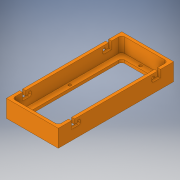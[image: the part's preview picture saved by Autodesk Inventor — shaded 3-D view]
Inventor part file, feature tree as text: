
AUTODESK INVENTOR PART (.ipt)
format: ipt  version: 2017 (Build 210142000, 142)  size: 281,088 bytes
history: native  units: in
note: dims shown in document units (in); Inventor stores cm internally (conversion verified against a paired STEP export)
features: extrude x4, sketch x3, fillet x3, plane x2, mirror x1, projected_geometry x1
ambient origin geometry x8: Origin, YZ Plane, XZ Plane, XY Plane, X Axis, Y Axis, Z Axis, Center Point
bodies: Solid1 (feature_tree)
feature tree (14):
  extrude  "Extrusion1"  Depth=0.125in
  sketch  "Sketch2"  dims[d2=0.125in d3=0.125in]
  extrude  "Extrusion9"  Depth=0.125in
  extrude  "Extrusion10"  Depth=0.125in
  extrude  "Extrusion11"  Depth=0.125in
  fillet  "Fillet1"  Radius=0.25in
  fillet  "Fillet2"  Radius=0.25in
  fillet  "Fillet3"  Radius=0.125in
  plane  "Work Plane1"
  mirror  "Mirror1"
  sketch  "Sketch9"  dims[d7=0.25in d8=0.125in]
  sketch  "Sketch10"  dims[d9=0.125in d10=0.125in d11=0.125in d12=0.25in d13=0.25in d14=0.125in d15=0.125in d16=0.25in d17=0.25in d18=0.125in d19=0.75in d20=0.0in d121=0.574in d154=1.0in d155=0.0in d156=0.25in d157=0.25in d158=0.25in d159=0.25in d160=0.125in d161=0.0in d163=0.125in d166=0.125in d167=4.75in d168=2.375in d169=0.125in d170=0.0625in d171=2.375in d172=0.125in d173=0.125in d174=1.75in d175=0.875in d176=0.125in d177=0.125in d178=0.9375in d179=0.125in d180=0.0in d181=0.125in d182=0.125in d183=0.125in d190=0.125in d191=0.125in d192=0.125in d193=0.125in d194=0.1in d195=0.1in d196=0.0625in d197=0.0625in]
  projected_geometry  "Projected Loop2"
  plane  "Work Plane2"
